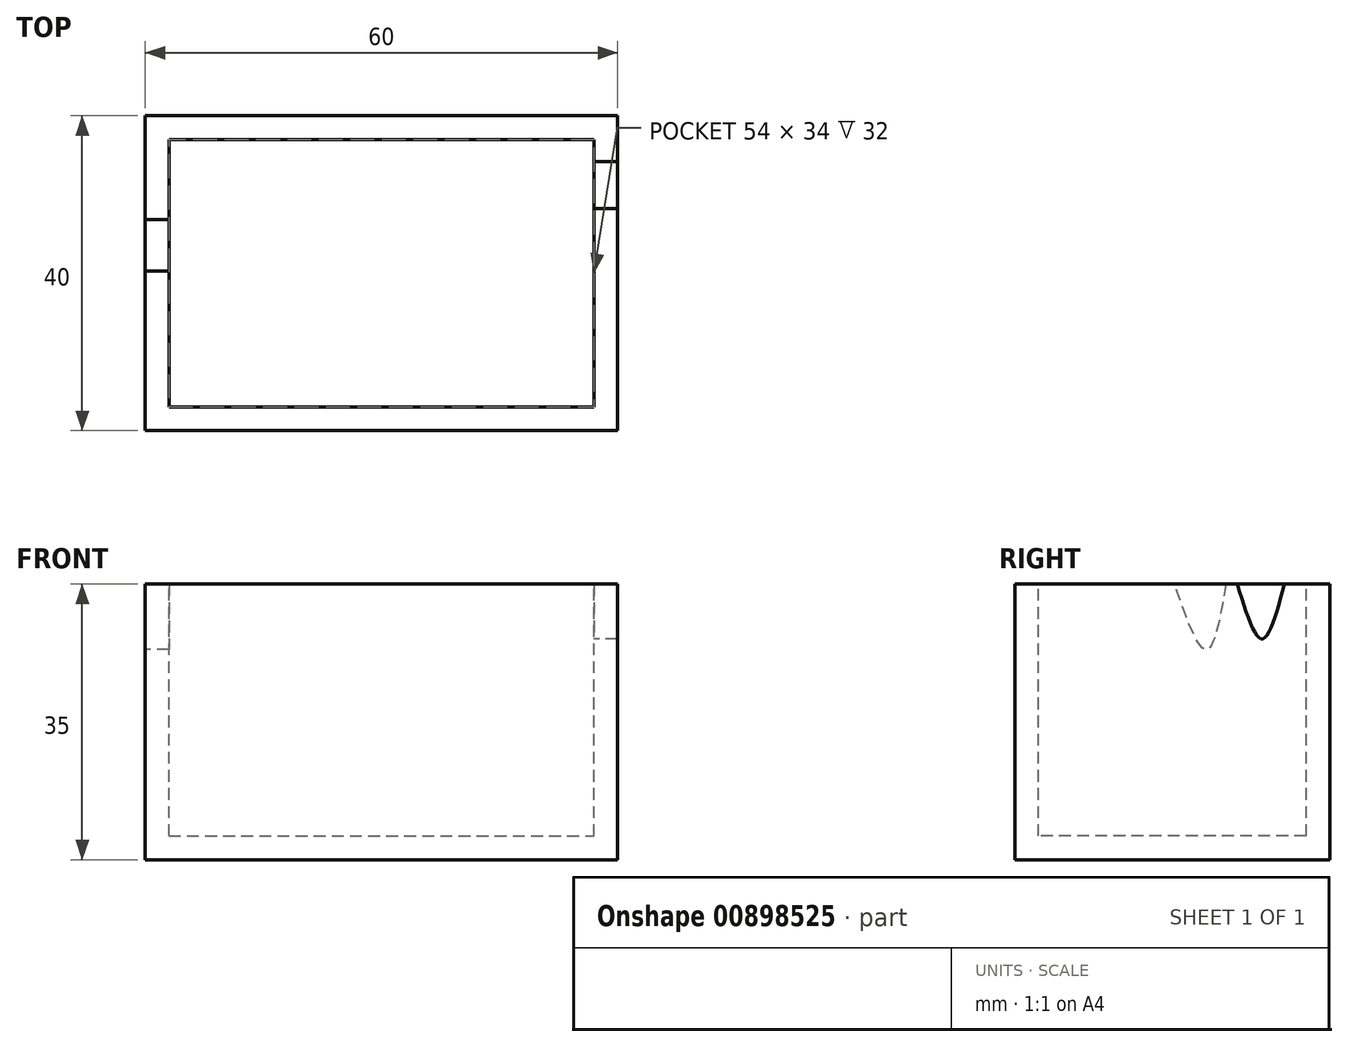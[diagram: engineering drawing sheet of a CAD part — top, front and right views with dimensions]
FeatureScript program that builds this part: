
annotation { "Feature Type Name" : "Feature", "Feature Type Description" : "" }
export const myFeature = defineFeature(function(context is Context, id is Id, definition is map)
    precondition{}
    {
        {
            var Q0;
            Q0=qCreatedBy(makeId("Top.planeOp"),FACE);
            var sketch = newSketch(context, id + "F0", { "sketchPlane" : qUnion([Q0])});
            skLineSegment(sketch, "E0.bottom", {"start": v(-30.16, 19.75) * mm, "end": v(29.84, 19.75) * mm});
            skLineSegment(sketch, "E0.top", {"start": v(-30.16, -20.25) * mm, "end": v(29.84, -20.25) * mm});
            skLineSegment(sketch, "E0.left", {"start": v(-30.16, 19.75) * mm, "end": v(-30.16, -20.25) * mm});
            skLineSegment(sketch, "E0.right", {"start": v(29.84, 19.75) * mm, "end": v(29.84, -20.25) * mm});
            skSolve(sketch);
        }
        {
            var Q0;
            Q0 = qSketchRegion(id + "F0", true);
            var Q1;
            Q1=makeQuery(id+"F0.imprint","IMPRINT",FACE,{"disambiguationData":[TD([[makeQuery(id+"F0.imprint","IMPRINT",EDGE,{"derivedFrom":sQuery(id+"F0.wireOp",EDGE,"E0.bottom")}),-1.0]])]});
            extrude(context, id + "F1", {"entities" : qUnion([Q0, Q1]), "depth" : 35 * mm, "offsetDistance" : 25 * mm});
        }
        {
            var Q0;
            Q0=makeQuery(id+"F1.opExtrude","CAP_FACE",FACE,{"disambiguationData":[OSD([sQuery(id+"F0.wireOp",EDGE,"E0.bottom"),sQuery(id+"F0.wireOp",EDGE,"E0.top"),sQuery(id+"F0.wireOp",EDGE,"E0.left"),sQuery(id+"F0.wireOp",EDGE,"E0.right")])],"isStart":false});
            var sketch = newSketch(context, id + "F2", { "sketchPlane" : qUnion([Q0])});
            skLineSegment(sketch, "E1.bottom", {"start": v(-27.16, 16.75) * mm, "end": v(26.84, 16.75) * mm});
            skLineSegment(sketch, "E1.top", {"start": v(-27.16, -17.25) * mm, "end": v(26.84, -17.25) * mm});
            skLineSegment(sketch, "E1.left", {"start": v(-27.16, 16.75) * mm, "end": v(-27.16, -17.25) * mm});
            skLineSegment(sketch, "E1.right", {"start": v(26.84, 16.75) * mm, "end": v(26.84, -17.25) * mm});
            skSolve(sketch);
        }
        {
            var Q0;
            Q0 = qSketchRegion(id + "F2", true);
            extrude(context, id + "F3", {"entities" : qUnion([Q0]), "operationType" : NewBodyOperationType.REMOVE, "oppositeDirection" : true, "depth" : 32 * mm, "offsetDistance" : 25 * mm});
        }
        {
            var Q0;
            Q0=makeQuery(id+"F1.opExtrude","SWEPT_FACE",FACE,{"disambiguationData":[OSD([sQuery(id+"F0.wireOp",EDGE,"E0.left")])]});
            var sketch = newSketch(context, id + "F4", { "sketchPlane" : qUnion([Q0])});
            skFitSpline(sketch, "E2", {"points": [v(-6.55, 35) * mm, v(-4.06, 26.7) * mm, v(0, 35) * mm], "startDerivative": vector(4.35, -25.07) * mm, "endDerivative": vector(8.73, 24.8) * mm});
            skSolve(sketch);
        }
        {
            var Q0;
            {var subQ0=sQuery(id+"F4.wireOp",EDGE,"E2");Q0=makeQuery(id+"F4.imprint","IMPRINT",FACE,{"disambiguationData":[TD([[makeQuery(id+"F4.imprint","IMPRINT",EDGE,{"derivedFrom":subQ0}),1.0]])]});}
            extrude(context, id + "F5", {"entities" : qUnion([Q0]), "operationType" : NewBodyOperationType.REMOVE, "oppositeDirection" : true, "depth" : 5 * mm, "offsetDistance" : 25 * mm});
        }
        {
            var Q0;
            Q0=makeQuery(id+"F1.opExtrude","SWEPT_FACE",FACE,{"disambiguationData":[OSD([sQuery(id+"F0.wireOp",EDGE,"E0.right")])]});
            var sketch = newSketch(context, id + "F6", { "sketchPlane" : qUnion([Q0])});
            skFitSpline(sketch, "E3", {"points": [v(7.98, 35) * mm, v(11.14, 28.05) * mm, v(13.96, 35) * mm], "startDerivative": vector(6.45, -20.81) * mm, "endDerivative": vector(5.5, 20.87) * mm});
            skSolve(sketch);
        }
        {
            var Q0;
            {var subQ0=sQuery(id+"F6.wireOp",EDGE,"E3");Q0=makeQuery(id+"F6.imprint","IMPRINT",FACE,{"disambiguationData":[TD([[makeQuery(id+"F6.imprint","IMPRINT",EDGE,{"derivedFrom":subQ0}),1.0]])]});}
            extrude(context, id + "F7", {"entities" : qUnion([Q0]), "operationType" : NewBodyOperationType.REMOVE, "oppositeDirection" : true, "depth" : 5 * mm, "offsetDistance" : 25 * mm});
        }
    });
